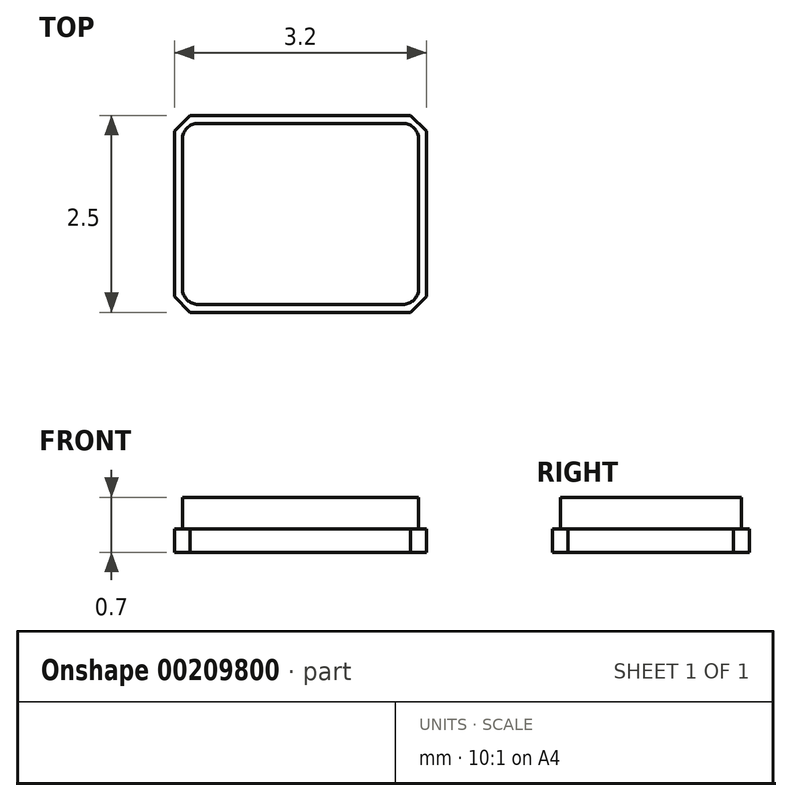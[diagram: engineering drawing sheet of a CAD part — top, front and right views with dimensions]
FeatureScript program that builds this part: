
annotation { "Feature Type Name" : "Feature", "Feature Type Description" : "" }
export const myFeature = defineFeature(function(context is Context, id is Id, definition is map)
    precondition{}
    {
        {
            var Q0;
            Q0=qCreatedBy(makeId("Top.planeOp"),FACE);
            var sketch = newSketch(context, id + "F0", { "sketchPlane" : qUnion([Q0]) });
            skLineSegment(sketch, "E0.bottom", {"start": v(-1.6, 1.25) * mm, "end": v(1.6, 1.25) * mm});
            skLineSegment(sketch, "E0.top", {"start": v(-1.6, -1.25) * mm, "end": v(1.6, -1.25) * mm});
            skLineSegment(sketch, "E0.left", {"start": v(-1.6, 1.25) * mm, "end": v(-1.6, -1.25) * mm});
            skLineSegment(sketch, "E0.right", {"start": v(1.6, 1.25) * mm, "end": v(1.6, -1.25) * mm});
            skLineSegment(sketch, "E1", {"start": v(0, 1.25) * mm, "end": v(0, -1.25) * mm, "construction": true});
            skSolve(sketch);
        }
        {
            var Q0;
            Q0=makeQuery(id+"F0.imprint","IMPRINT",FACE,{"disambiguationData":[TD([[makeQuery(id+"F0.imprint","IMPRINT",EDGE,{"derivedFrom":sQuery(id+"F0.wireOp",EDGE,"E0.bottom")}),-1.0]])]});
            extrude(context, id + "F1", {"entities" : qUnion([Q0]), "depth" : 0.3 * mm});
        }
        {
            var Q0;
            Q0=makeQuery(id+"F1.opExtrude","CAP_FACE",FACE,{"disambiguationData":[OSD([sQuery(id+"F0.wireOp",EDGE,"E0.bottom"),sQuery(id+"F0.wireOp",EDGE,"E0.top"),sQuery(id+"F0.wireOp",EDGE,"E0.left"),sQuery(id+"F0.wireOp",EDGE,"E0.right")])],"isStart":false});
            var sketch = newSketch(context, id + "F2", { "sketchPlane" : qUnion([Q0]) });
            skLineSegment(sketch, "E2.0", {"start": v(1.5, 1.15) * mm, "end": v(-1.5, 1.15) * mm});
            skLineSegment(sketch, "E2.1", {"start": v(1.5, -1.15) * mm, "end": v(1.5, 1.15) * mm});
            skLineSegment(sketch, "E2.2", {"start": v(-1.5, -1.15) * mm, "end": v(1.5, -1.15) * mm});
            skLineSegment(sketch, "E2.3", {"start": v(-1.5, 1.15) * mm, "end": v(-1.5, -1.15) * mm});
            skSolve(sketch);
        }
        {
            var Q0;
            Q0=makeQuery(id+"F2.imprint","IMPRINT",FACE,{"disambiguationData":[TD([[makeQuery(id+"F2.imprint","IMPRINT",EDGE,{"derivedFrom":sQuery(id+"F2.wireOp",EDGE,"E2.0")}),1.0]])]});
            extrude(context, id + "F3", {"entities" : qUnion([Q0]), "operationType" : NewBodyOperationType.ADD, "depth" : 0.4 * mm});
        }
        {
            var Q0;
            Q0=makeQuery(id+"F3.opExtrude","SWEPT_EDGE",EDGE,{"disambiguationData":[OSD([sQuery(id+"F2.wireOp",EDGE,"E2.0"),sQuery(id+"F2.wireOp",EDGE,"E2.1")])]});
            var Q1;
            Q1=makeQuery(id+"F3.opExtrude","SWEPT_EDGE",EDGE,{"disambiguationData":[OSD([sQuery(id+"F2.wireOp",EDGE,"E2.1"),sQuery(id+"F2.wireOp",EDGE,"E2.2")])]});
            var Q2;
            Q2=makeQuery(id+"F3.opExtrude","SWEPT_EDGE",EDGE,{"disambiguationData":[OSD([sQuery(id+"F2.wireOp",EDGE,"E2.2"),sQuery(id+"F2.wireOp",EDGE,"E2.3")])]});
            var Q3;
            Q3=makeQuery(id+"F3.opExtrude","SWEPT_EDGE",EDGE,{"disambiguationData":[OSD([sQuery(id+"F2.wireOp",EDGE,"E2.0"),sQuery(id+"F2.wireOp",EDGE,"E2.3")])]});
            fillet(context, id + "F4", {"entities" : qUnion([Q0, Q1, Q2, Q3]), "radius" : 0.2 * mm, "tangentPropagation" : true, "conicFillet" : false});
        }
        {
            var Q0;
            Q0=makeQuery(id+"F1.opExtrude","SWEPT_EDGE",EDGE,{"disambiguationData":[OSD([sQuery(id+"F0.wireOp",EDGE,"E0.top"),sQuery(id+"F0.wireOp",EDGE,"E0.left")])]});
            var Q1;
            Q1=makeQuery(id+"F1.opExtrude","SWEPT_EDGE",EDGE,{"disambiguationData":[OSD([sQuery(id+"F0.wireOp",EDGE,"E0.bottom"),sQuery(id+"F0.wireOp",EDGE,"E0.left")])]});
            var Q2;
            Q2=makeQuery(id+"F1.opExtrude","SWEPT_EDGE",EDGE,{"disambiguationData":[OSD([sQuery(id+"F0.wireOp",EDGE,"E0.top"),sQuery(id+"F0.wireOp",EDGE,"E0.right")])]});
            var Q3;
            Q3=makeQuery(id+"F1.opExtrude","SWEPT_EDGE",EDGE,{"disambiguationData":[OSD([sQuery(id+"F0.wireOp",EDGE,"E0.bottom"),sQuery(id+"F0.wireOp",EDGE,"E0.right")])]});
            chamfer(context, id + "F5", {"entities" : qUnion([Q0, Q1, Q2, Q3]), "width" : 0.2 * mm, "tangentPropagation" : true});
        }
    });
